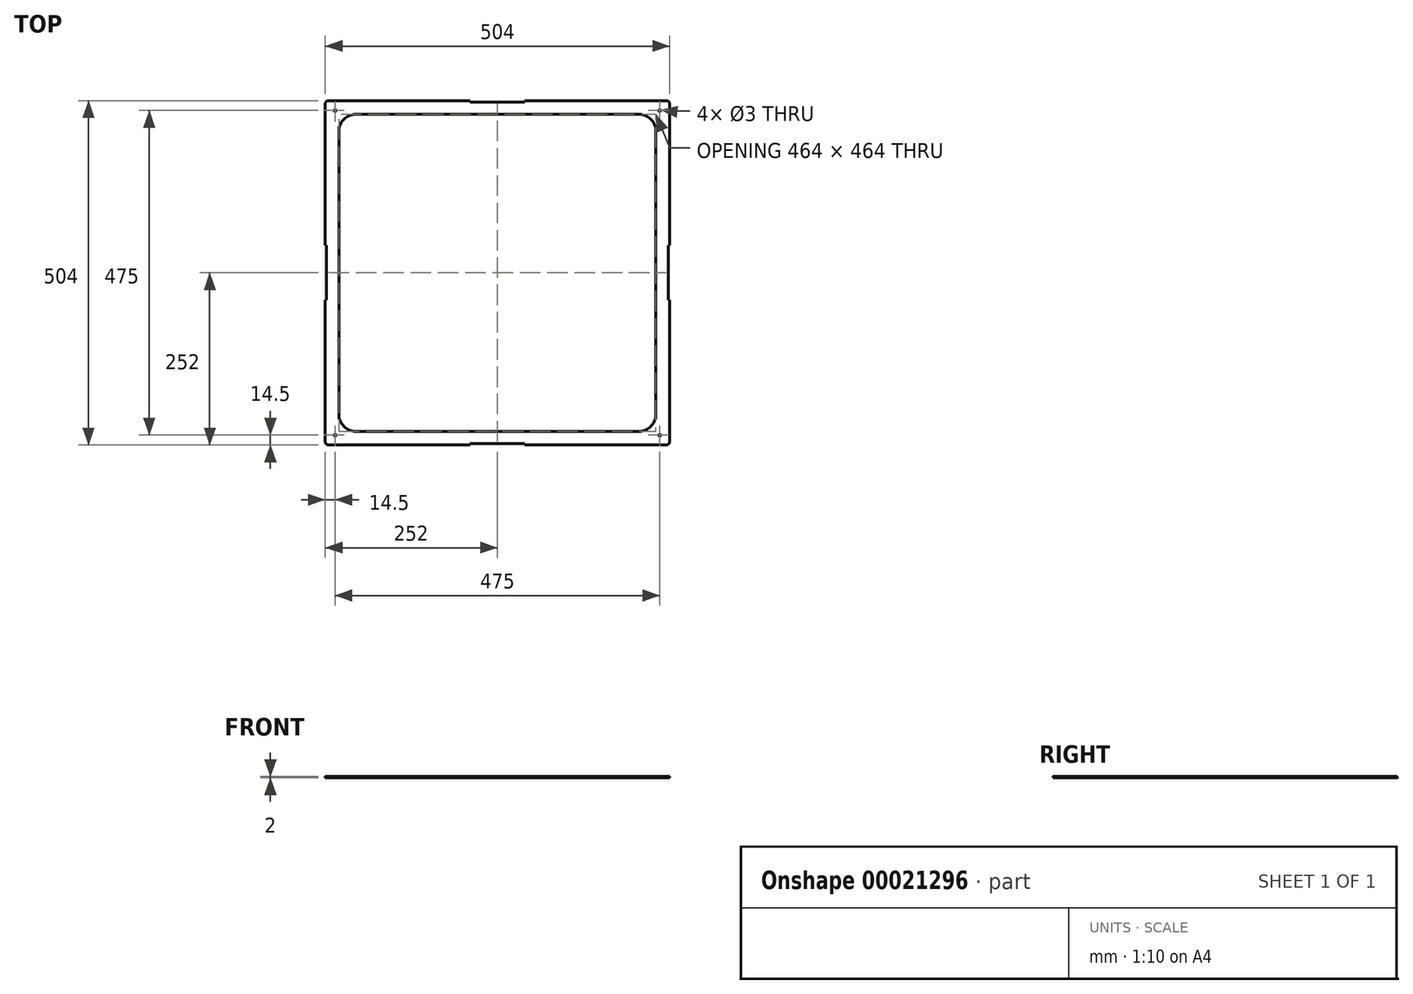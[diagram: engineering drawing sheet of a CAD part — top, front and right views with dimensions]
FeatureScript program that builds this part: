
annotation { "Feature Type Name" : "Feature", "Feature Type Description" : "" }
export const myFeature = defineFeature(function(context is Context, id is Id, definition is map)
    precondition{}
    {
        {
            var Q0;
            Q0=qCreatedBy(makeId("Top.planeOp"),FACE);
            var sketch = newSketch(context, id + "F0", { "sketchPlane" : qUnion([Q0])});
            skLineSegment(sketch, "E0.rect.bottom", {"start": v(252, 252) * mm, "end": v(-252, 252) * mm});
            skLineSegment(sketch, "E0.rect.top", {"start": v(252, -252) * mm, "end": v(-252, -252) * mm});
            skLineSegment(sketch, "E0.rect.left", {"start": v(252, 252) * mm, "end": v(252, -252) * mm});
            skLineSegment(sketch, "E0.rect.right", {"start": v(-252, 252) * mm, "end": v(-252, -252) * mm});
            skPoint(sketch, "E0.rect.middle", {"position": v(0, 0) * mm});
            skLineSegment(sketch, "E1.rect.bottom", {"start": v(232, 232) * mm, "end": v(-232, 232) * mm});
            skLineSegment(sketch, "E1.rect.top", {"start": v(232, -232) * mm, "end": v(-232, -232) * mm});
            skLineSegment(sketch, "E1.rect.left", {"start": v(232, 232) * mm, "end": v(232, -232) * mm});
            skLineSegment(sketch, "E1.rect.right", {"start": v(-232, 232) * mm, "end": v(-232, -232) * mm});
            skSolve(sketch);
        }
        {
            var Q0;
            Q0=makeQuery(id+"F0.imprint","IMPRINT",FACE,{"disambiguationData":[TD([[makeQuery(id+"F0.imprint","IMPRINT",EDGE,{"derivedFrom":sQuery(id+"F0.wireOp",EDGE,"E0.rect.bottom")}),1.0]])]});
            extrude(context, id + "F1", {"entities" : qUnion([Q0]), "depth" : 2 * mm});
        }
        {
            var Q0;
            Q0=makeQuery(id+"F1.opExtrude","CAP_FACE",FACE,{"disambiguationData":[OSD([sQuery(id+"F0.wireOp",EDGE,"E0.rect.bottom"),sQuery(id+"F0.wireOp",EDGE,"E0.rect.top"),sQuery(id+"F0.wireOp",EDGE,"E0.rect.left"),sQuery(id+"F0.wireOp",EDGE,"E0.rect.right"),sQuery(id+"F0.wireOp",EDGE,"E1.rect.bottom"),sQuery(id+"F0.wireOp",EDGE,"E1.rect.top"),sQuery(id+"F0.wireOp",EDGE,"E1.rect.left"),sQuery(id+"F0.wireOp",EDGE,"E1.rect.right")])],"isStart":false});
            var sketch = newSketch(context, id + "F2", { "sketchPlane" : qUnion([Q0])});
            skLineSegment(sketch, "E2.rect.bottom", {"start": v(40, -250) * mm, "end": v(-40, -250) * mm});
            skLineSegment(sketch, "E2.rect.top", {"start": v(40, -254) * mm, "end": v(-40, -254) * mm});
            skLineSegment(sketch, "E2.rect.left", {"start": v(40, -250) * mm, "end": v(40, -254) * mm});
            skLineSegment(sketch, "E2.rect.right", {"start": v(-40, -250) * mm, "end": v(-40, -254) * mm});
            skPoint(sketch, "E2.rect.middle", {"position": v(0, -252) * mm});
            skLineSegment(sketch, "E3.rect.bottom", {"start": v(254, -40) * mm, "end": v(250, -40) * mm});
            skLineSegment(sketch, "E3.rect.top", {"start": v(254, 40) * mm, "end": v(250, 40) * mm});
            skLineSegment(sketch, "E3.rect.left", {"start": v(254, -40) * mm, "end": v(254, 40) * mm});
            skLineSegment(sketch, "E3.rect.right", {"start": v(250, -40) * mm, "end": v(250, 40) * mm});
            skPoint(sketch, "E3.rect.middle", {"position": v(252, 0) * mm});
            skLineSegment(sketch, "E4.rect.bottom", {"start": v(40, 254) * mm, "end": v(-40, 254) * mm});
            skLineSegment(sketch, "E4.rect.top", {"start": v(40, 250) * mm, "end": v(-40, 250) * mm});
            skLineSegment(sketch, "E4.rect.left", {"start": v(40, 254) * mm, "end": v(40, 250) * mm});
            skLineSegment(sketch, "E4.rect.right", {"start": v(-40, 254) * mm, "end": v(-40, 250) * mm});
            skPoint(sketch, "E4.rect.middle", {"position": v(0, 252) * mm});
            skLineSegment(sketch, "E5.rect.bottom", {"start": v(-250, -40) * mm, "end": v(-254, -40) * mm});
            skLineSegment(sketch, "E5.rect.top", {"start": v(-250, 40) * mm, "end": v(-254, 40) * mm});
            skLineSegment(sketch, "E5.rect.left", {"start": v(-250, -40) * mm, "end": v(-250, 40) * mm});
            skLineSegment(sketch, "E5.rect.right", {"start": v(-254, -40) * mm, "end": v(-254, 40) * mm});
            skPoint(sketch, "E5.rect.middle", {"position": v(-252, 0) * mm});
            skSolve(sketch);
        }
        {
            var Q0;
            Q0 = qSketchRegion(id + "F2", true);
            extrude(context, id + "F3", {"entities" : qUnion([Q0]), "operationType" : NewBodyOperationType.REMOVE, "oppositeDirection" : true, "depth" : 25 * mm});
        }
        {
            var Q0;
            Q0=makeQuery(id+"F1.opExtrude","SWEPT_EDGE",EDGE,{"disambiguationData":[OSD([sQuery(id+"F0.wireOp",EDGE,"E1.rect.bottom"),sQuery(id+"F0.wireOp",EDGE,"E1.rect.right")])]});
            var Q1;
            Q1=makeQuery(id+"F1.opExtrude","SWEPT_EDGE",EDGE,{"disambiguationData":[OSD([sQuery(id+"F0.wireOp",EDGE,"E1.rect.bottom"),sQuery(id+"F0.wireOp",EDGE,"E1.rect.left")])]});
            var Q2;
            Q2=makeQuery(id+"F1.opExtrude","SWEPT_EDGE",EDGE,{"disambiguationData":[OSD([sQuery(id+"F0.wireOp",EDGE,"E1.rect.top"),sQuery(id+"F0.wireOp",EDGE,"E1.rect.left")])]});
            var Q3;
            Q3=makeQuery(id+"F1.opExtrude","SWEPT_EDGE",EDGE,{"disambiguationData":[OSD([sQuery(id+"F0.wireOp",EDGE,"E1.rect.top"),sQuery(id+"F0.wireOp",EDGE,"E1.rect.right")])]});
            fillet(context, id + "F4", {"entities" : qUnion([Q0, Q1, Q2, Q3]), "radius" : 25 * mm, "tangentPropagation" : true, "allowEdgeOverflow" : false});
        }
        {
            var Q0;
            Q0=makeQuery(id+"F1.opExtrude","SWEPT_EDGE",EDGE,{"disambiguationData":[OSD([sQuery(id+"F0.wireOp",EDGE,"E0.rect.top"),sQuery(id+"F0.wireOp",EDGE,"E0.rect.right")])]});
            var Q1;
            Q1=makeQuery(id+"F1.opExtrude","SWEPT_EDGE",EDGE,{"disambiguationData":[OSD([sQuery(id+"F0.wireOp",EDGE,"E0.rect.top"),sQuery(id+"F0.wireOp",EDGE,"E0.rect.left")])]});
            var Q2;
            Q2=makeQuery(id+"F1.opExtrude","SWEPT_EDGE",EDGE,{"disambiguationData":[OSD([sQuery(id+"F0.wireOp",EDGE,"E0.rect.bottom"),sQuery(id+"F0.wireOp",EDGE,"E0.rect.left")])]});
            var Q3;
            Q3=makeQuery(id+"F1.opExtrude","SWEPT_EDGE",EDGE,{"disambiguationData":[OSD([sQuery(id+"F0.wireOp",EDGE,"E0.rect.bottom"),sQuery(id+"F0.wireOp",EDGE,"E0.rect.right")])]});
            fillet(context, id + "F5", {"entities" : qUnion([Q0, Q1, Q2, Q3]), "radius" : 5 * mm, "tangentPropagation" : true, "allowEdgeOverflow" : false});
        }
        {
            var Q0;
            Q0=makeQuery(id+"F1.opExtrude","CAP_FACE",FACE,{"disambiguationData":[OSD([sQuery(id+"F0.wireOp",EDGE,"E0.rect.bottom"),sQuery(id+"F0.wireOp",EDGE,"E0.rect.top"),sQuery(id+"F0.wireOp",EDGE,"E0.rect.left"),sQuery(id+"F0.wireOp",EDGE,"E0.rect.right"),sQuery(id+"F0.wireOp",EDGE,"E1.rect.bottom"),sQuery(id+"F0.wireOp",EDGE,"E1.rect.top"),sQuery(id+"F0.wireOp",EDGE,"E1.rect.left"),sQuery(id+"F0.wireOp",EDGE,"E1.rect.right")])],"isStart":false});
            var sketch = newSketch(context, id + "F6", { "sketchPlane" : qUnion([Q0])});
            skLineSegment(sketch, "E6.rect.bottom", {"start": v(-237.5, -237.5) * mm, "end": v(237.5, -237.5) * mm, "construction": true});
            skLineSegment(sketch, "E6.rect.top", {"start": v(-237.5, 237.5) * mm, "end": v(237.5, 237.5) * mm, "construction": true});
            skLineSegment(sketch, "E6.rect.left", {"start": v(-237.5, -237.5) * mm, "end": v(-237.5, 237.5) * mm, "construction": true});
            skLineSegment(sketch, "E6.rect.right", {"start": v(237.5, -237.5) * mm, "end": v(237.5, 237.5) * mm, "construction": true});
            skPoint(sketch, "E6.rect.middle", {"position": v(0, 0) * mm});
            skCircle(sketch, "E7", {"center": v(-237.5, 237.5) * mm, "radius": 1.5 * mm});
            skCircle(sketch, "E8", {"center": v(237.5, 237.5) * mm, "radius": 1.5 * mm});
            skCircle(sketch, "E9", {"center": v(237.5, -237.5) * mm, "radius": 1.5 * mm});
            skCircle(sketch, "E10", {"center": v(-237.5, -237.5) * mm, "radius": 1.5 * mm});
            skSolve(sketch);
        }
        {
            var Q0;
            Q0 = qSketchRegion(id + "F6", true);
            extrude(context, id + "F7", {"entities" : qUnion([Q0]), "operationType" : NewBodyOperationType.REMOVE, "oppositeDirection" : true, "depth" : 25 * mm});
        }
    });
